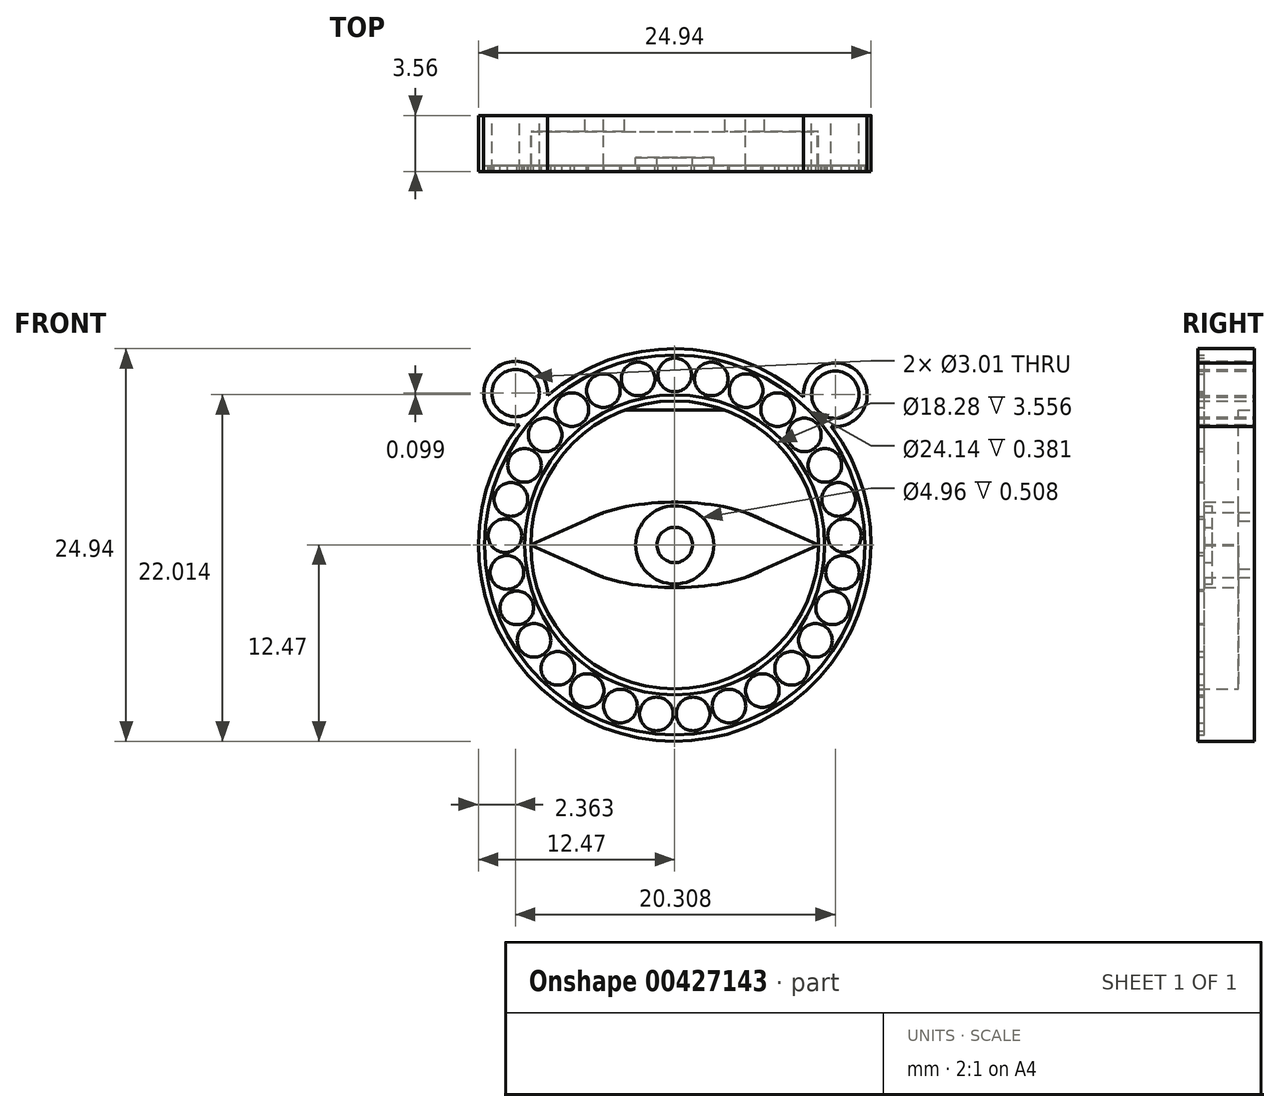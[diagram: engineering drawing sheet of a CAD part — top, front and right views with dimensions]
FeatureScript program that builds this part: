
annotation { "Feature Type Name" : "Feature", "Feature Type Description" : "" }
export const myFeature = defineFeature(function(context is Context, id is Id, definition is map)
    precondition{}
    {
        {
            var Q0;
            Q0=qCreatedBy(makeId("Front.planeOp"),FACE);
            var sketch = newSketch(context, id + "F0", { "sketchPlane" : qUnion([Q0])});
            skCircle(sketch, "E0", {"center": v(0, 0) * mm, "radius": 9.53 * mm});
            skCircle(sketch, "E1", {"center": v(0, 0) * mm, "radius": 12.07 * mm});
            skEllipse(sketch, "E2", {"center": v(0, 0) * mm, "majorRadius": 6.9 * mm, "minorRadius": 2.71 * mm, "majorAxis": v(1, 0)});
            skLineSegment(sketch, "E3", {"start": v(0, 9.53) * mm, "end": v(0, 12.07) * mm});
            skCircle(sketch, "E4", {"center": v(0, 10.8) * mm, "radius": 1.07 * mm});
            skCircle(sketch, "E5.1.0", {"center": v(2.32, 10.54) * mm, "radius": 1.07 * mm});
            skCircle(sketch, "E5.2.0", {"center": v(4.53, 9.8) * mm, "radius": 1.07 * mm});
            skCircle(sketch, "E5.3.0", {"center": v(6.53, 8.6) * mm, "radius": 1.07 * mm});
            skCircle(sketch, "E5.4.0", {"center": v(8.23, 7) * mm, "radius": 1.07 * mm});
            skCircle(sketch, "E5.5.0", {"center": v(9.54, 5.06) * mm, "radius": 1.07 * mm});
            skCircle(sketch, "E5.6.0", {"center": v(10.4, 2.89) * mm, "radius": 1.07 * mm});
            skCircle(sketch, "E5.7.0", {"center": v(10.78, 0.58) * mm, "radius": 1.07 * mm});
            skCircle(sketch, "E5.8.0", {"center": v(10.66, -1.75) * mm, "radius": 1.07 * mm});
            skCircle(sketch, "E5.9.0", {"center": v(10.03, -4) * mm, "radius": 1.07 * mm});
            skCircle(sketch, "E5.10.0", {"center": v(8.94, -6.06) * mm, "radius": 1.07 * mm});
            skCircle(sketch, "E5.11.0", {"center": v(7.43, -7.84) * mm, "radius": 1.07 * mm});
            skCircle(sketch, "E5.12.0", {"center": v(5.57, -9.25) * mm, "radius": 1.07 * mm});
            skCircle(sketch, "E5.13.0", {"center": v(3.45, -10.23) * mm, "radius": 1.07 * mm});
            skCircle(sketch, "E5.14.0", {"center": v(1.17, -10.73) * mm, "radius": 1.07 * mm});
            skCircle(sketch, "E5.15.0", {"center": v(-1.17, -10.73) * mm, "radius": 1.07 * mm});
            skCircle(sketch, "E5.16.0", {"center": v(-3.45, -10.23) * mm, "radius": 1.07 * mm});
            skCircle(sketch, "E5.17.0", {"center": v(-5.57, -9.25) * mm, "radius": 1.07 * mm});
            skCircle(sketch, "E5.18.0", {"center": v(-7.43, -7.84) * mm, "radius": 1.07 * mm});
            skCircle(sketch, "E5.19.0", {"center": v(-8.94, -6.06) * mm, "radius": 1.07 * mm});
            skCircle(sketch, "E5.20.0", {"center": v(-10.03, -4) * mm, "radius": 1.07 * mm});
            skCircle(sketch, "E5.21.0", {"center": v(-10.66, -1.75) * mm, "radius": 1.07 * mm});
            skCircle(sketch, "E5.22.0", {"center": v(-10.78, 0.58) * mm, "radius": 1.07 * mm});
            skCircle(sketch, "E5.23.0", {"center": v(-10.4, 2.89) * mm, "radius": 1.07 * mm});
            skCircle(sketch, "E5.24.0", {"center": v(-9.54, 5.06) * mm, "radius": 1.07 * mm});
            skCircle(sketch, "E5.25.0", {"center": v(-8.23, 7) * mm, "radius": 1.07 * mm});
            skCircle(sketch, "E5.26.0", {"center": v(-6.53, 8.6) * mm, "radius": 1.07 * mm});
            skCircle(sketch, "E5.27.0", {"center": v(-4.53, 9.8) * mm, "radius": 1.07 * mm});
            skCircle(sketch, "E5.28.0", {"center": v(-2.32, 10.54) * mm, "radius": 1.07 * mm});
            skLineSegment(sketch, "E5.anchor1", {"start": v(0, 0) * mm, "end": v(0, 10.8) * mm, "construction": true});
            skLineSegment(sketch, "E5.anchor2", {"start": v(0, 0) * mm, "end": v(-2.32, 10.54) * mm, "construction": true});
            skCircle(sketch, "E6", {"center": v(0, 0) * mm, "radius": 2.48 * mm});
            skCircle(sketch, "E7", {"center": v(0, 0) * mm, "radius": 1.12 * mm});
            skCircle(sketch, "E8", {"center": v(0, 0) * mm, "radius": 12.47 * mm});
            skCircle(sketch, "E9", {"center": v(0, 0) * mm, "radius": 9.14 * mm});
            skLineSegment(sketch, "E10", {"start": v(-9.14, 0) * mm, "end": v(-4.51, 2.05) * mm});
            skLineSegment(sketch, "E11", {"start": v(-4.51, -2.05) * mm, "end": v(-9.14, 0) * mm});
            skLineSegment(sketch, "E12", {"start": v(4.51, -2.05) * mm, "end": v(9.14, 0) * mm});
            skLineSegment(sketch, "E13", {"start": v(9.14, 0) * mm, "end": v(4.51, 2.05) * mm});
            skLineSegment(sketch, "E14", {"start": v(-9.08, 0.03) * mm, "end": v(-9.14, 0.03) * mm});
            skLineSegment(sketch, "E15", {"start": v(-9.08, 0.03) * mm, "end": v(-9.08, -0.03) * mm});
            skLineSegment(sketch, "E16", {"start": v(-9.08, -0.03) * mm, "end": v(-9.14, -0.03) * mm});
            skLineSegment(sketch, "E17", {"start": v(9.08, -0.03) * mm, "end": v(9.08, 0.03) * mm});
            skLineSegment(sketch, "E18", {"start": v(9.08, 0.03) * mm, "end": v(9.14, 0.03) * mm});
            skLineSegment(sketch, "E19", {"start": v(9.08, -0.03) * mm, "end": v(9.14, -0.03) * mm});
            skCircle(sketch, "E20", {"center": v(-10.1, 9.64) * mm, "radius": 1.5 * mm});
            skPoint(sketch, "E20.first.point", {"position": v(-9.06, 8.57) * mm});
            skPoint(sketch, "E20.second.point", {"position": v(-11.25, 10.62) * mm});
            skPoint(sketch, "E20.third.point", {"position": v(-9.27, 10.9) * mm});
            skLineSegment(sketch, "E21", {"start": v(-9.06, 8.57) * mm, "end": v(9.06, 8.57) * mm});
            skCircle(sketch, "E22", {"center": v(10.2, 9.54) * mm, "radius": 1.5 * mm});
            skPoint(sketch, "E22.second.point", {"position": v(11.49, 10.33) * mm});
            skPoint(sketch, "E22.third.point", {"position": v(11.7, 9.69) * mm});
            skCircle(sketch, "E23", {"center": v(-10.1, 9.64) * mm, "radius": 2.02 * mm});
            skCircle(sketch, "E24", {"center": v(10.2, 9.54) * mm, "radius": 2.02 * mm});
            skSolve(sketch);
        }
        {
            var Q0;
            Q0=makeQuery(id+"F0.imprint","IMPRINT",FACE,{"disambiguationData":[TD([[makeQuery(id+"F0.imprint","IMPRINT",EDGE,{"derivedFrom":sQuery(id+"F0.wireOp",EDGE,"E0")}),-1.0]])]});
            var Q1;
            Q1=makeQuery(id+"F0.imprint","IMPRINT",FACE,{"disambiguationData":[TD([[makeQuery(id+"F0.imprint","IMPRINT",EDGE,{"derivedFrom":sQuery(id+"F0.wireOp",EDGE,"E5.4.0")}),-1.0]])]});
            var Q2;
            {var subQ0=sQuery(id+"F0.wireOp",EDGE,"E21");var subQ1=sQuery(id+"F0.wireOp",EDGE,"E1");var subQ2=makeQuery(id+"F0.imprint","INTERSECT",VERTEX,{"disambiguationData":[OD(1.0)],"derivedFrom":[subQ1,subQ0]});Q2=makeQuery(id+"F0.imprint","IMPRINT",FACE,{"disambiguationData":[TD([[makeQuery(id+"F0.imprint","IMPRINT",EDGE,{"disambiguationData":[TD([[subQ2,-1.0]])],"derivedFrom":subQ1}),1.0]])]});}
            var Q3;
            {var subQ0=sQuery(id+"F0.wireOp",EDGE,"E21");var subQ1=sQuery(id+"F0.wireOp",EDGE,"E1");var subQ2=makeQuery(id+"F0.imprint","INTERSECT",VERTEX,{"disambiguationData":[OD(0.0)],"derivedFrom":[subQ1,subQ0]});Q3=makeQuery(id+"F0.imprint","IMPRINT",FACE,{"disambiguationData":[TD([[makeQuery(id+"F0.imprint","IMPRINT",EDGE,{"disambiguationData":[TD([[subQ2,1.0]])],"derivedFrom":subQ1}),1.0]])]});}
            var Q4;
            {var subQ0=sQuery(id+"F0.wireOp",EDGE,"E21");var subQ1=sQuery(id+"F0.wireOp",EDGE,"E1");var subQ2=makeQuery(id+"F0.imprint","INTERSECT",VERTEX,{"disambiguationData":[OD(0.0)],"derivedFrom":[subQ1,subQ0]});Q4=makeQuery(id+"F0.imprint","IMPRINT",FACE,{"disambiguationData":[TD([[makeQuery(id+"F0.imprint","IMPRINT",EDGE,{"disambiguationData":[TD([[subQ2,-1.0]])],"derivedFrom":subQ1}),1.0]])]});}
            var Q5;
            {var subQ0=sQuery(id+"F0.wireOp",EDGE,"E23");var subQ1=sQuery(id+"F0.wireOp",EDGE,"E1");var subQ2=makeQuery(id+"F0.imprint","INTERSECT",VERTEX,{"disambiguationData":[OD(0.0)],"derivedFrom":[subQ1,subQ0]});Q5=makeQuery(id+"F0.imprint","IMPRINT",FACE,{"disambiguationData":[TD([[makeQuery(id+"F0.imprint","IMPRINT",EDGE,{"disambiguationData":[TD([[subQ2,-1.0]])],"derivedFrom":subQ1}),1.0]])]});}
            extrude(context, id + "F1", {"entities" : qUnion([Q0, Q1, Q2, Q3, Q4, Q5]), "depth" : 3.17 * mm});
        }
        {
            var Q0;
            {var subQ2=sQuery(id+"F0.wireOp",EDGE,"E21");var subQ7=sQuery(id+"F0.wireOp",EDGE,"E0");var subQ9=makeQuery(id+"F0.imprint","INTERSECT",VERTEX,{"disambiguationData":[OD(0.0)],"derivedFrom":[subQ7,subQ2]});Q0=makeQuery(id+"F0.imprint","IMPRINT",FACE,{"disambiguationData":[TD([[makeQuery(id+"F0.imprint","IMPRINT",EDGE,{"disambiguationData":[TD([[subQ9,1.0]])],"derivedFrom":subQ7}),1.0]])]});}
            var Q1;
            {var subQ0=sQuery(id+"F0.wireOp",EDGE,"E24");var subQ1=sQuery(id+"F0.wireOp",EDGE,"E1");var subQ2=makeQuery(id+"F0.imprint","INTERSECT",VERTEX,{"disambiguationData":[OD(0.0)],"derivedFrom":[subQ1,subQ0]});Q1=makeQuery(id+"F0.imprint","IMPRINT",FACE,{"disambiguationData":[TD([[makeQuery(id+"F0.imprint","IMPRINT",EDGE,{"disambiguationData":[TD([[subQ2,1.0]])],"derivedFrom":subQ1}),-1.0]])]});}
            var Q2;
            {var subQ4=sQuery(id+"F0.wireOp",EDGE,"E1");var subQ7=sQuery(id+"F0.wireOp",EDGE,"E23");var subQ9=makeQuery(id+"F0.imprint","INTERSECT",VERTEX,{"disambiguationData":[OD(0.0)],"derivedFrom":[subQ4,subQ7]});Q2=makeQuery(id+"F0.imprint","IMPRINT",FACE,{"disambiguationData":[TD([[makeQuery(id+"F0.imprint","IMPRINT",EDGE,{"disambiguationData":[TD([[subQ9,-1.0]])],"derivedFrom":subQ4}),-1.0]])]});}
            var Q3;
            {var subQ0=sQuery(id+"F0.wireOp",EDGE,"E21");var subQ1=sQuery(id+"F0.wireOp",EDGE,"E1");var subQ2=makeQuery(id+"F0.imprint","INTERSECT",VERTEX,{"disambiguationData":[OD(1.0)],"derivedFrom":[subQ1,subQ0]});Q3=makeQuery(id+"F0.imprint","IMPRINT",FACE,{"disambiguationData":[TD([[makeQuery(id+"F0.imprint","IMPRINT",EDGE,{"disambiguationData":[TD([[subQ2,-1.0]])],"derivedFrom":subQ1}),-1.0]])]});}
            var Q4;
            {var subQ3=sQuery(id+"F0.wireOp",EDGE,"E1");var subQ7=makeQuery(id+"F0.imprint","INTERSECT",VERTEX,{"derivedFrom":[subQ3,sQuery(id+"F0.wireOp",EDGE,"E3")]});Q4=makeQuery(id+"F0.imprint","IMPRINT",FACE,{"disambiguationData":[TD([[makeQuery(id+"F0.imprint","IMPRINT",EDGE,{"disambiguationData":[TD([[subQ7,1.0]])],"derivedFrom":subQ3}),-1.0]])]});}
            var Q5;
            {var subQ1=sQuery(id+"F0.wireOp",EDGE,"E21");var subQ7=sQuery(id+"F0.wireOp",EDGE,"E1");var subQ8=makeQuery(id+"F0.imprint","INTERSECT",VERTEX,{"disambiguationData":[OD(0.0)],"derivedFrom":[subQ7,subQ1]});Q5=makeQuery(id+"F0.imprint","IMPRINT",FACE,{"disambiguationData":[TD([[makeQuery(id+"F0.imprint","IMPRINT",EDGE,{"disambiguationData":[TD([[subQ8,1.0]])],"derivedFrom":subQ7}),-1.0]])]});}
            var Q6;
            {var subQ0=sQuery(id+"F0.wireOp",EDGE,"E21");var subQ1=sQuery(id+"F0.wireOp",EDGE,"E1");var subQ2=makeQuery(id+"F0.imprint","INTERSECT",VERTEX,{"disambiguationData":[OD(0.0)],"derivedFrom":[subQ1,subQ0]});Q6=makeQuery(id+"F0.imprint","IMPRINT",FACE,{"disambiguationData":[TD([[makeQuery(id+"F0.imprint","IMPRINT",EDGE,{"disambiguationData":[TD([[subQ2,-1.0]])],"derivedFrom":subQ1}),-1.0]])]});}
            var Q7;
            {var subQ0=sQuery(id+"F0.wireOp",EDGE,"E23");var subQ1=sQuery(id+"F0.wireOp",EDGE,"E8");var subQ2=makeQuery(id+"F0.imprint","INTERSECT",VERTEX,{"disambiguationData":[OD(0.0)],"derivedFrom":[subQ1,subQ0]});Q7=makeQuery(id+"F0.imprint","IMPRINT",FACE,{"disambiguationData":[TD([[makeQuery(id+"F0.imprint","IMPRINT",EDGE,{"disambiguationData":[TD([[subQ2,-1.0]])],"derivedFrom":subQ1}),-1.0]])]});}
            var Q8;
            {var subQ0=sQuery(id+"F0.wireOp",EDGE,"E24");var subQ1=sQuery(id+"F0.wireOp",EDGE,"E8");var subQ2=makeQuery(id+"F0.imprint","INTERSECT",VERTEX,{"disambiguationData":[OD(0.0)],"derivedFrom":[subQ1,subQ0]});Q8=makeQuery(id+"F0.imprint","IMPRINT",FACE,{"disambiguationData":[TD([[makeQuery(id+"F0.imprint","IMPRINT",EDGE,{"disambiguationData":[TD([[subQ2,-1.0]])],"derivedFrom":subQ1}),-1.0]])]});}
            extrude(context, id + "F2", {"entities" : qUnion([Q0, Q1, Q2, Q3, Q4, Q5, Q6, Q7, Q8]), "operationType" : NewBodyOperationType.ADD, "depth" : 3.56 * mm});
        }
        {
            var Q0;
            Q0=makeQuery(id+"F0.imprint","IMPRINT",FACE,{"disambiguationData":[TD([[makeQuery(id+"F0.imprint","IMPRINT",EDGE,{"derivedFrom":sQuery(id+"F0.wireOp",EDGE,"E5.23.0")}),1.0]])]});
            var Q1;
            Q1=makeQuery(id+"F0.imprint","IMPRINT",FACE,{"disambiguationData":[TD([[makeQuery(id+"F0.imprint","IMPRINT",EDGE,{"derivedFrom":sQuery(id+"F0.wireOp",EDGE,"E5.24.0")}),1.0]])]});
            var Q2;
            Q2=makeQuery(id+"F0.imprint","IMPRINT",FACE,{"disambiguationData":[TD([[makeQuery(id+"F0.imprint","IMPRINT",EDGE,{"derivedFrom":sQuery(id+"F0.wireOp",EDGE,"E5.25.0")}),1.0]])]});
            var Q3;
            Q3=makeQuery(id+"F0.imprint","IMPRINT",FACE,{"disambiguationData":[TD([[makeQuery(id+"F0.imprint","IMPRINT",EDGE,{"derivedFrom":sQuery(id+"F0.wireOp",EDGE,"E5.26.0")}),1.0]])]});
            var Q4;
            Q4=makeQuery(id+"F0.imprint","IMPRINT",FACE,{"disambiguationData":[TD([[makeQuery(id+"F0.imprint","IMPRINT",EDGE,{"derivedFrom":sQuery(id+"F0.wireOp",EDGE,"E5.27.0")}),1.0]])]});
            var Q5;
            Q5=makeQuery(id+"F0.imprint","IMPRINT",FACE,{"disambiguationData":[TD([[makeQuery(id+"F0.imprint","IMPRINT",EDGE,{"derivedFrom":sQuery(id+"F0.wireOp",EDGE,"E5.28.0")}),1.0]])]});
            var Q6;
            {var subQ0=sQuery(id+"F0.wireOp",EDGE,"E4");var subQ1=sQuery(id+"F0.wireOp",EDGE,"E3");var subQ2=makeQuery(id+"F0.imprint","INTERSECT",VERTEX,{"disambiguationData":[OD(0.0)],"derivedFrom":[subQ1,subQ0]});Q6=makeQuery(id+"F0.imprint","IMPRINT",FACE,{"disambiguationData":[TD([[makeQuery(id+"F0.imprint","IMPRINT",EDGE,{"disambiguationData":[TD([[subQ2,-1.0]])],"derivedFrom":subQ1}),1.0]])]});}
            var Q7;
            {var subQ0=sQuery(id+"F0.wireOp",EDGE,"E4");var subQ1=sQuery(id+"F0.wireOp",EDGE,"E3");var subQ2=makeQuery(id+"F0.imprint","INTERSECT",VERTEX,{"disambiguationData":[OD(0.0)],"derivedFrom":[subQ1,subQ0]});Q7=makeQuery(id+"F0.imprint","IMPRINT",FACE,{"disambiguationData":[TD([[makeQuery(id+"F0.imprint","IMPRINT",EDGE,{"disambiguationData":[TD([[subQ2,-1.0]])],"derivedFrom":subQ1}),-1.0]])]});}
            var Q8;
            Q8=makeQuery(id+"F0.imprint","IMPRINT",FACE,{"disambiguationData":[TD([[makeQuery(id+"F0.imprint","IMPRINT",EDGE,{"derivedFrom":sQuery(id+"F0.wireOp",EDGE,"E5.1.0")}),1.0]])]});
            var Q9;
            Q9=makeQuery(id+"F0.imprint","IMPRINT",FACE,{"disambiguationData":[TD([[makeQuery(id+"F0.imprint","IMPRINT",EDGE,{"derivedFrom":sQuery(id+"F0.wireOp",EDGE,"E5.2.0")}),1.0]])]});
            var Q10;
            Q10=makeQuery(id+"F0.imprint","IMPRINT",FACE,{"disambiguationData":[TD([[makeQuery(id+"F0.imprint","IMPRINT",EDGE,{"derivedFrom":sQuery(id+"F0.wireOp",EDGE,"E5.3.0")}),1.0]])]});
            var Q11;
            Q11=makeQuery(id+"F0.imprint","IMPRINT",FACE,{"disambiguationData":[TD([[makeQuery(id+"F0.imprint","IMPRINT",EDGE,{"derivedFrom":sQuery(id+"F0.wireOp",EDGE,"E5.4.0")}),1.0]])]});
            var Q12;
            Q12=makeQuery(id+"F0.imprint","IMPRINT",FACE,{"disambiguationData":[TD([[makeQuery(id+"F0.imprint","IMPRINT",EDGE,{"derivedFrom":sQuery(id+"F0.wireOp",EDGE,"E5.5.0")}),1.0]])]});
            var Q13;
            Q13=makeQuery(id+"F0.imprint","IMPRINT",FACE,{"disambiguationData":[TD([[makeQuery(id+"F0.imprint","IMPRINT",EDGE,{"derivedFrom":sQuery(id+"F0.wireOp",EDGE,"E5.6.0")}),1.0]])]});
            var Q14;
            Q14=makeQuery(id+"F0.imprint","IMPRINT",FACE,{"disambiguationData":[TD([[makeQuery(id+"F0.imprint","IMPRINT",EDGE,{"derivedFrom":sQuery(id+"F0.wireOp",EDGE,"E5.7.0")}),1.0]])]});
            var Q15;
            Q15=makeQuery(id+"F0.imprint","IMPRINT",FACE,{"disambiguationData":[TD([[makeQuery(id+"F0.imprint","IMPRINT",EDGE,{"derivedFrom":sQuery(id+"F0.wireOp",EDGE,"E5.8.0")}),1.0]])]});
            var Q16;
            Q16=makeQuery(id+"F0.imprint","IMPRINT",FACE,{"disambiguationData":[TD([[makeQuery(id+"F0.imprint","IMPRINT",EDGE,{"derivedFrom":sQuery(id+"F0.wireOp",EDGE,"E5.9.0")}),1.0]])]});
            var Q17;
            Q17=makeQuery(id+"F0.imprint","IMPRINT",FACE,{"disambiguationData":[TD([[makeQuery(id+"F0.imprint","IMPRINT",EDGE,{"derivedFrom":sQuery(id+"F0.wireOp",EDGE,"E5.10.0")}),1.0]])]});
            var Q18;
            Q18=makeQuery(id+"F0.imprint","IMPRINT",FACE,{"disambiguationData":[TD([[makeQuery(id+"F0.imprint","IMPRINT",EDGE,{"derivedFrom":sQuery(id+"F0.wireOp",EDGE,"E5.11.0")}),1.0]])]});
            var Q19;
            Q19=makeQuery(id+"F0.imprint","IMPRINT",FACE,{"disambiguationData":[TD([[makeQuery(id+"F0.imprint","IMPRINT",EDGE,{"derivedFrom":sQuery(id+"F0.wireOp",EDGE,"E5.12.0")}),1.0]])]});
            var Q20;
            Q20=makeQuery(id+"F0.imprint","IMPRINT",FACE,{"disambiguationData":[TD([[makeQuery(id+"F0.imprint","IMPRINT",EDGE,{"derivedFrom":sQuery(id+"F0.wireOp",EDGE,"E5.13.0")}),1.0]])]});
            var Q21;
            Q21=makeQuery(id+"F0.imprint","IMPRINT",FACE,{"disambiguationData":[TD([[makeQuery(id+"F0.imprint","IMPRINT",EDGE,{"derivedFrom":sQuery(id+"F0.wireOp",EDGE,"E5.14.0")}),1.0]])]});
            var Q22;
            Q22=makeQuery(id+"F0.imprint","IMPRINT",FACE,{"disambiguationData":[TD([[makeQuery(id+"F0.imprint","IMPRINT",EDGE,{"derivedFrom":sQuery(id+"F0.wireOp",EDGE,"E5.15.0")}),1.0]])]});
            var Q23;
            Q23=makeQuery(id+"F0.imprint","IMPRINT",FACE,{"disambiguationData":[TD([[makeQuery(id+"F0.imprint","IMPRINT",EDGE,{"derivedFrom":sQuery(id+"F0.wireOp",EDGE,"E5.16.0")}),1.0]])]});
            var Q24;
            Q24=makeQuery(id+"F0.imprint","IMPRINT",FACE,{"disambiguationData":[TD([[makeQuery(id+"F0.imprint","IMPRINT",EDGE,{"derivedFrom":sQuery(id+"F0.wireOp",EDGE,"E5.17.0")}),1.0]])]});
            var Q25;
            Q25=makeQuery(id+"F0.imprint","IMPRINT",FACE,{"disambiguationData":[TD([[makeQuery(id+"F0.imprint","IMPRINT",EDGE,{"derivedFrom":sQuery(id+"F0.wireOp",EDGE,"E5.18.0")}),1.0]])]});
            var Q26;
            Q26=makeQuery(id+"F0.imprint","IMPRINT",FACE,{"disambiguationData":[TD([[makeQuery(id+"F0.imprint","IMPRINT",EDGE,{"derivedFrom":sQuery(id+"F0.wireOp",EDGE,"E5.19.0")}),1.0]])]});
            var Q27;
            Q27=makeQuery(id+"F0.imprint","IMPRINT",FACE,{"disambiguationData":[TD([[makeQuery(id+"F0.imprint","IMPRINT",EDGE,{"derivedFrom":sQuery(id+"F0.wireOp",EDGE,"E5.20.0")}),1.0]])]});
            var Q28;
            Q28=makeQuery(id+"F0.imprint","IMPRINT",FACE,{"disambiguationData":[TD([[makeQuery(id+"F0.imprint","IMPRINT",EDGE,{"derivedFrom":sQuery(id+"F0.wireOp",EDGE,"E5.21.0")}),1.0]])]});
            var Q29;
            Q29=makeQuery(id+"F0.imprint","IMPRINT",FACE,{"disambiguationData":[TD([[makeQuery(id+"F0.imprint","IMPRINT",EDGE,{"derivedFrom":sQuery(id+"F0.wireOp",EDGE,"E5.22.0")}),1.0]])]});
            var Q30;
            {var subQ1=sQuery(id+"F0.wireOp",EDGE,"E0");var subQ5=makeQuery(id+"F0.imprint","INTERSECT",VERTEX,{"derivedFrom":[subQ1,sQuery(id+"F0.wireOp",EDGE,"E3")]});Q30=makeQuery(id+"F0.imprint","IMPRINT",FACE,{"disambiguationData":[TD([[makeQuery(id+"F0.imprint","IMPRINT",EDGE,{"disambiguationData":[TD([[subQ5,1.0]])],"derivedFrom":subQ1}),1.0]])]});}
            extrude(context, id + "F3", {"entities" : qUnion([Q0, Q1, Q2, Q3, Q4, Q5, Q6, Q7, Q8, Q9, Q10, Q11, Q12, Q13, Q14, Q15, Q16, Q17, Q18, Q19, Q20, Q21, Q22, Q23, Q24, Q25, Q26, Q27, Q28, Q29, Q30]), "operationType" : NewBodyOperationType.ADD, "depth" : 3.56 * mm});
        }
        {
            var Q0;
            {var subQ5=sQuery(id+"F0.wireOp",EDGE,"E15");Q0=makeQuery(id+"F0.imprint","IMPRINT",FACE,{"disambiguationData":[TD([[makeQuery(id+"F0.imprint","IMPRINT",EDGE,{"derivedFrom":subQ5}),1.0]])]});}
            var Q1;
            {var subQ3=sQuery(id+"F0.wireOp",EDGE,"E15");Q1=makeQuery(id+"F0.imprint","IMPRINT",FACE,{"disambiguationData":[TD([[makeQuery(id+"F0.imprint","IMPRINT",EDGE,{"derivedFrom":subQ3}),-1.0]])]});}
            var Q2;
            {var subQ3=sQuery(id+"F0.wireOp",EDGE,"E16");Q2=makeQuery(id+"F0.imprint","IMPRINT",FACE,{"disambiguationData":[TD([[makeQuery(id+"F0.imprint","IMPRINT",EDGE,{"derivedFrom":subQ3}),-1.0]])]});}
            var Q3;
            {var subQ3=sQuery(id+"F0.wireOp",EDGE,"E14");Q3=makeQuery(id+"F0.imprint","IMPRINT",FACE,{"disambiguationData":[TD([[makeQuery(id+"F0.imprint","IMPRINT",EDGE,{"derivedFrom":subQ3}),1.0]])]});}
            var Q4;
            {var subQ3=sQuery(id+"F0.wireOp",EDGE,"E18");Q4=makeQuery(id+"F0.imprint","IMPRINT",FACE,{"disambiguationData":[TD([[makeQuery(id+"F0.imprint","IMPRINT",EDGE,{"derivedFrom":subQ3}),-1.0]])]});}
            var Q5;
            {var subQ3=sQuery(id+"F0.wireOp",EDGE,"E19");Q5=makeQuery(id+"F0.imprint","IMPRINT",FACE,{"disambiguationData":[TD([[makeQuery(id+"F0.imprint","IMPRINT",EDGE,{"derivedFrom":subQ3}),1.0]])]});}
            var Q6;
            {var subQ3=sQuery(id+"F0.wireOp",EDGE,"E17");Q6=makeQuery(id+"F0.imprint","IMPRINT",FACE,{"disambiguationData":[TD([[makeQuery(id+"F0.imprint","IMPRINT",EDGE,{"derivedFrom":subQ3}),-1.0]])]});}
            var Q7;
            {var subQ5=sQuery(id+"F0.wireOp",EDGE,"E17");Q7=makeQuery(id+"F0.imprint","IMPRINT",FACE,{"disambiguationData":[TD([[makeQuery(id+"F0.imprint","IMPRINT",EDGE,{"derivedFrom":subQ5}),1.0]])]});}
            var Q8;
            Q8=makeQuery(id+"F0.imprint","IMPRINT",FACE,{"disambiguationData":[TD([[makeQuery(id+"F0.imprint","IMPRINT",EDGE,{"derivedFrom":sQuery(id+"F0.wireOp",EDGE,"E6")}),-1.0]])]});
            extrude(context, id + "F4", {"entities" : qUnion([Q0, Q1, Q2, Q3, Q4, Q5, Q6, Q7, Q8]), "operationType" : NewBodyOperationType.ADD, "depth" : 3.17 * mm});
        }
        {
            var Q0;
            Q0=makeQuery(id+"F0.imprint","IMPRINT",FACE,{"disambiguationData":[TD([[makeQuery(id+"F0.imprint","IMPRINT",EDGE,{"derivedFrom":sQuery(id+"F0.wireOp",EDGE,"E6")}),1.0]])]});
            extrude(context, id + "F5", {"entities" : qUnion([Q0]), "operationType" : NewBodyOperationType.ADD, "depth" : 2.67 * mm});
        }
        {
            var Q0;
            Q0=makeQuery(id+"F0.imprint","IMPRINT",FACE,{"disambiguationData":[TD([[makeQuery(id+"F0.imprint","IMPRINT",EDGE,{"derivedFrom":sQuery(id+"F0.wireOp",EDGE,"E7")}),1.0]])]});
            extrude(context, id + "F6", {"entities" : qUnion([Q0]), "operationType" : NewBodyOperationType.ADD, "depth" : 3.17 * mm});
        }
        {
            var Q0;
            {var subQ0=sQuery(id+"F0.wireOp",EDGE,"E14");Q0=makeQuery(id+"F0.imprint","IMPRINT",FACE,{"disambiguationData":[TD([[makeQuery(id+"F0.imprint","IMPRINT",EDGE,{"derivedFrom":subQ0}),-1.0]])]});}
            var Q1;
            {var subQ0=sQuery(id+"F0.wireOp",EDGE,"E16");Q1=makeQuery(id+"F0.imprint","IMPRINT",FACE,{"disambiguationData":[TD([[makeQuery(id+"F0.imprint","IMPRINT",EDGE,{"derivedFrom":subQ0}),1.0]])]});}
            var Q2;
            {var subQ0=sQuery(id+"F0.wireOp",EDGE,"E21");var subQ1=sQuery(id+"F0.wireOp",EDGE,"E9");var subQ2=makeQuery(id+"F0.imprint","INTERSECT",VERTEX,{"disambiguationData":[OD(0.0)],"derivedFrom":[subQ1,subQ0]});Q2=makeQuery(id+"F0.imprint","IMPRINT",FACE,{"disambiguationData":[TD([[makeQuery(id+"F0.imprint","IMPRINT",EDGE,{"disambiguationData":[TD([[subQ2,-1.0]])],"derivedFrom":subQ1}),1.0]])]});}
            extrude(context, id + "F7", {"entities" : qUnion([Q0, Q1, Q2]), "operationType" : NewBodyOperationType.ADD, "depth" : 1.02 * mm});
        }
    });
